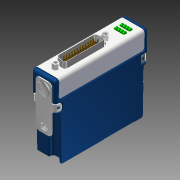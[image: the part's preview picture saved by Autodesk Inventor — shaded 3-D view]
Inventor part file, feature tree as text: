
AUTODESK INVENTOR PART (.ipt)
format: ipt  version: 2011 (Build 150239000, 239)  size: 6,503,936 bytes
history: native  units: mm
features: other x3, imported_body x1, sketch x1, fillet x1, extrude x1
ambient origin geometry x8: Origin, YZ Plane, XZ Plane, XY Plane, X Axis, Y Axis, Z Axis, Center Point
bodies: Solid1 (feature_tree)
feature tree (7):
  imported_body  "Base1"
  other  "RIGHT"
  other  "TOP"
  other  "FRONT"
  sketch  "Sketch2"  dims[d0=25.4mm d1=2.54mm d3=10.0mm d5=130.0mm d6=25.4mm d7=2.54mm d9=10.0mm d11=120.0mm d12=1.397mm d13=1.397mm d14=1.27mm d15=1.008245mm d17=0.0mm d18=25.4mm d19=0.381mm]
  fillet  "Fillet1"  [1 undecoded]
  extrude  "Extrusion1"  [1 undecoded]
note: 2 required parameter values undecoded (feature->parameter linkage not recoverable at this tier; creation-order binding heuristic only, values carry confidence <= 0.55)
